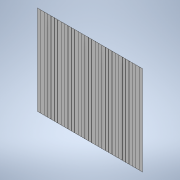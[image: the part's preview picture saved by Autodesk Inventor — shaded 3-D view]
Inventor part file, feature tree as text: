
AUTODESK INVENTOR PART (.ipt)
format: ipt  version: 2021 (Build 250183000, 183)  size: 222,208 bytes
history: native  units: in
note: dims shown in document units (in); Inventor stores cm internally (conversion verified against a paired STEP export)
features: extrude x3, sketch x3, pattern_linear x1, projected_geometry x1
ambient origin geometry x8: Origin, YZ Plane, XZ Plane, XY Plane, X Axis, Y Axis, Z Axis, Center Point
bodies: Solid1 (feature_tree)
feature tree (8):
  extrude  "Extrusion1"  Depth=2.742in
  extrude  "Extrusion2"  Depth=0.1in
  pattern_linear  "Rectangular Pattern1"  Count1=31 Spacing1=0.104in
  extrude  "Extrusion3"  Depth=0.104in TaperAngle=0.0deg
  sketch  "Sketch1"  dims[d0=4.0in d1=2.742in]
  sketch  "Sketch2"  dims[d2=0.04in d3=0.0in d4=0.1in]
  projected_geometry  "Projected Loop1"
  sketch  "Sketch3"  dims[d5=0.0015in d6=0.0in d7=12.2047in d9=0.104in d10=1.0in d11=0.0in]
